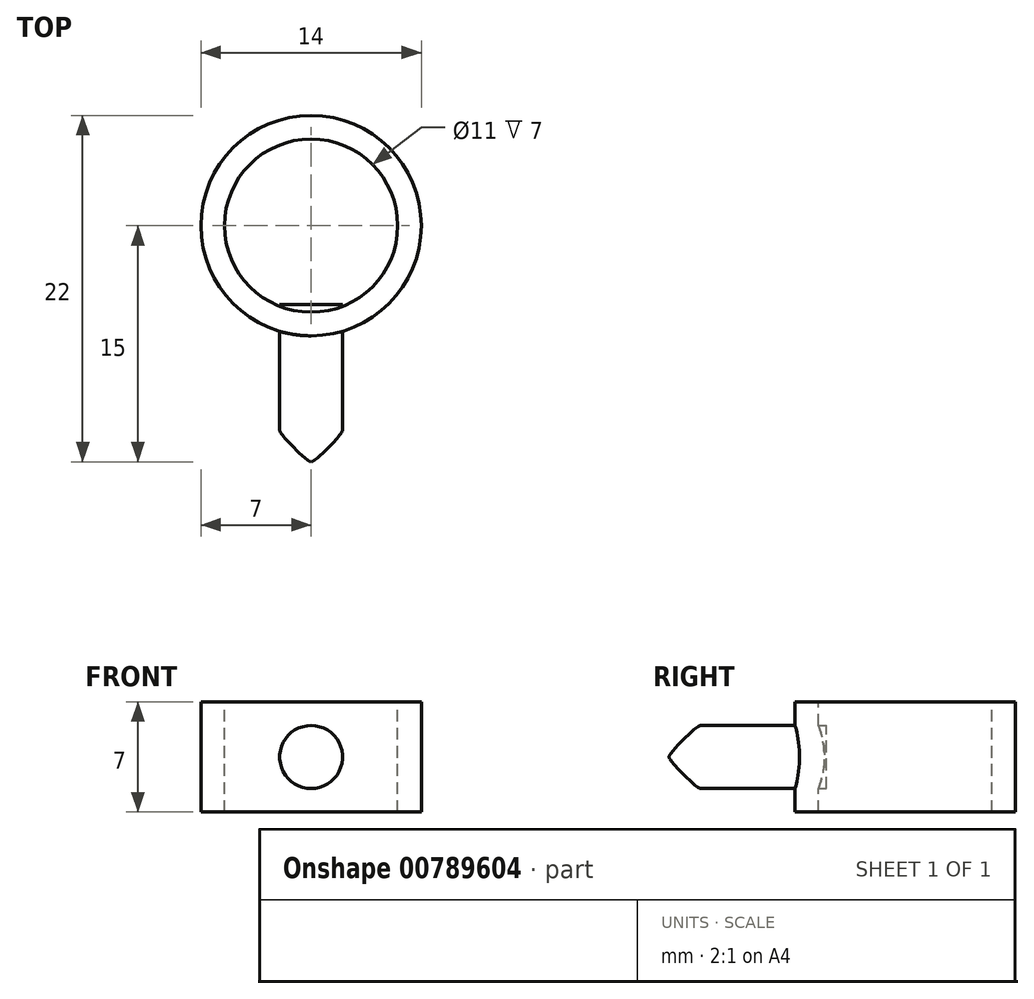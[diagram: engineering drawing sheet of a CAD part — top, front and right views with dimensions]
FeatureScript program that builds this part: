
annotation { "Feature Type Name" : "Feature", "Feature Type Description" : "" }
export const myFeature = defineFeature(function(context is Context, id is Id, definition is map)
    precondition{}
    {
        {
            var Q0;
            Q0=qCreatedBy(makeId("Top.planeOp"),FACE);
            var sketch = newSketch(context, id + "F0", { "sketchPlane" : qUnion([Q0])});
            skCircle(sketch, "E0", {"center": v(0, 0) * mm, "radius": 7 * mm});
            skCircle(sketch, "E1", {"center": v(0, 0) * mm, "radius": 5.5 * mm});
            skSolve(sketch);
        }
        {
            var Q0;
            Q0=makeQuery(id+"F0.imprint","IMPRINT",FACE,{"disambiguationData":[TD([[makeQuery(id+"F0.imprint","IMPRINT",EDGE,{"derivedFrom":sQuery(id+"F0.wireOp",EDGE,"E0")}),1.0]])]});
            extrude(context, id + "F1", {"entities" : qUnion([Q0]), "oppositeDirection" : true, "depth" : 7 * mm, "offsetDistance" : 25 * mm});
        }
        {
            var Q0;
            Q0=qCreatedBy(makeId("Front.planeOp"),FACE);
            var sketch = newSketch(context, id + "F2", { "sketchPlane" : qUnion([Q0])});
            skLineSegment(sketch, "E2", {"start": v(0, 0) * mm, "end": v(0, -7.42) * mm, "construction": true});
            skLineSegment(sketch, "E3", {"start": v(-5.5, 0) * mm, "end": v(6, -7.3) * mm, "construction": true});
            skLineSegment(sketch, "E4", {"start": v(6, -7.3) * mm, "end": v(5.5, 0) * mm, "construction": true});
            skLineSegment(sketch, "E5", {"start": v(5.5, 0) * mm, "end": v(-5.6, -7.07) * mm, "construction": true});
            skPoint(sketch, "E6", {"position": v(0, -3.5) * mm});
            skCircle(sketch, "E7", {"center": v(0, -3.5) * mm, "radius": 2 * mm});
            skSolve(sketch);
        }
        {
            var Q0;
            Q0 = qSketchRegion(id + "F2", true);
            extrude(context, id + "F3", {"entities" : qUnion([Q0]), "operationType" : NewBodyOperationType.ADD, "depth" : 15 * mm, "offsetDistance" : 25 * mm});
        }
        {
            var Q0;
            Q0=makeQuery(id+"F3.opExtrude","CAP_FACE",FACE,{"disambiguationData":[OSD([sQuery(id+"F2.wireOp",EDGE,"E7")])],"isStart":true});
            extrude(context, id + "F4", {"entities" : qUnion([Q0]), "operationType" : NewBodyOperationType.REMOVE, "oppositeDirection" : true, "depth" : 5 * mm, "offsetDistance" : 25 * mm});
        }
        {
            var Q0;
            Q0=makeQuery(id+"F3.opExtrude","CAP_FACE",FACE,{"disambiguationData":[OSD([sQuery(id+"F2.wireOp",EDGE,"E7")])],"isStart":false});
            fillet(context, id + "F5", {"entities" : qUnion([Q0]), "radius" : 2 * mm, "tangentPropagation" : true, "rho" : .1, "crossSection" : FilletCrossSection.CONIC, "allowEdgeOverflow" : false});
        }
    });
